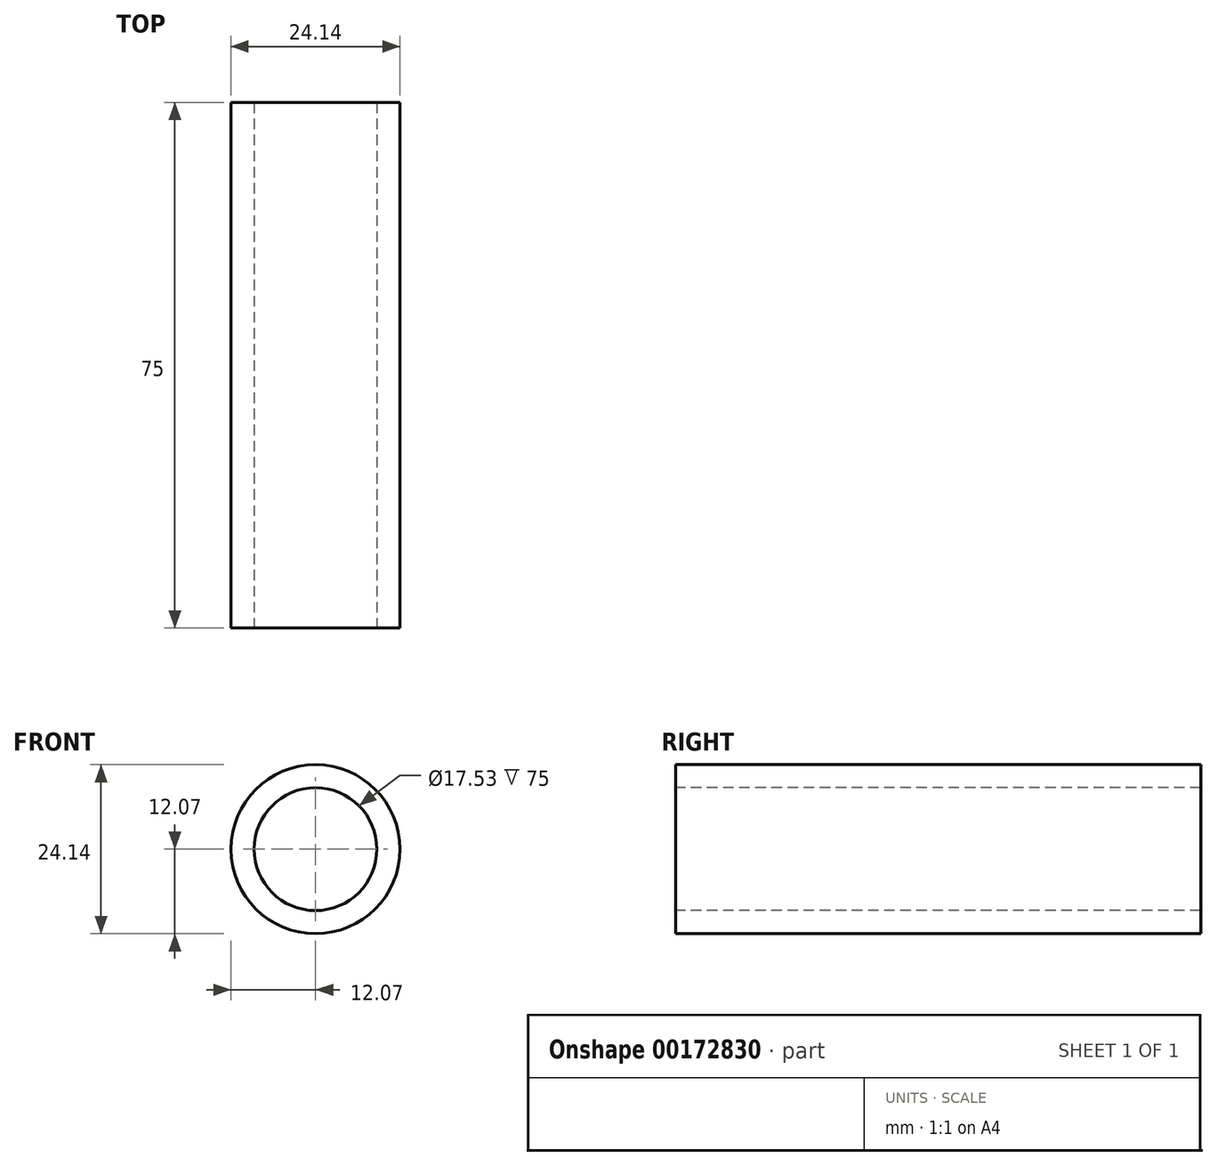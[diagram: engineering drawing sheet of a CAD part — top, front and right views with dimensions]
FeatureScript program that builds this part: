
annotation { "Feature Type Name" : "Feature", "Feature Type Description" : "" }
export const myFeature = defineFeature(function(context is Context, id is Id, definition is map)
    precondition{}
    {
        {
            var Q0;
            Q0=qCreatedBy(makeId("Front.planeOp"),FACE);
            var sketch = newSketch(context, id + "F0", { "sketchPlane" : qUnion([Q0])});
            skCircle(sketch, "E0", {"center": v(0, 0) * mm, "radius": 12.07 * mm});
            skCircle(sketch, "E1", {"center": v(0, 0) * mm, "radius": 8.76 * mm});
            skSolve(sketch);
        }
        {
            var Q0;
            Q0 = qSketchRegion(id + "F0", true);
            extrude(context, id + "F1", {"entities" : qUnion([Q0]), "oppositeDirection" : true, "depth" : 75 * mm});
        }
    });
